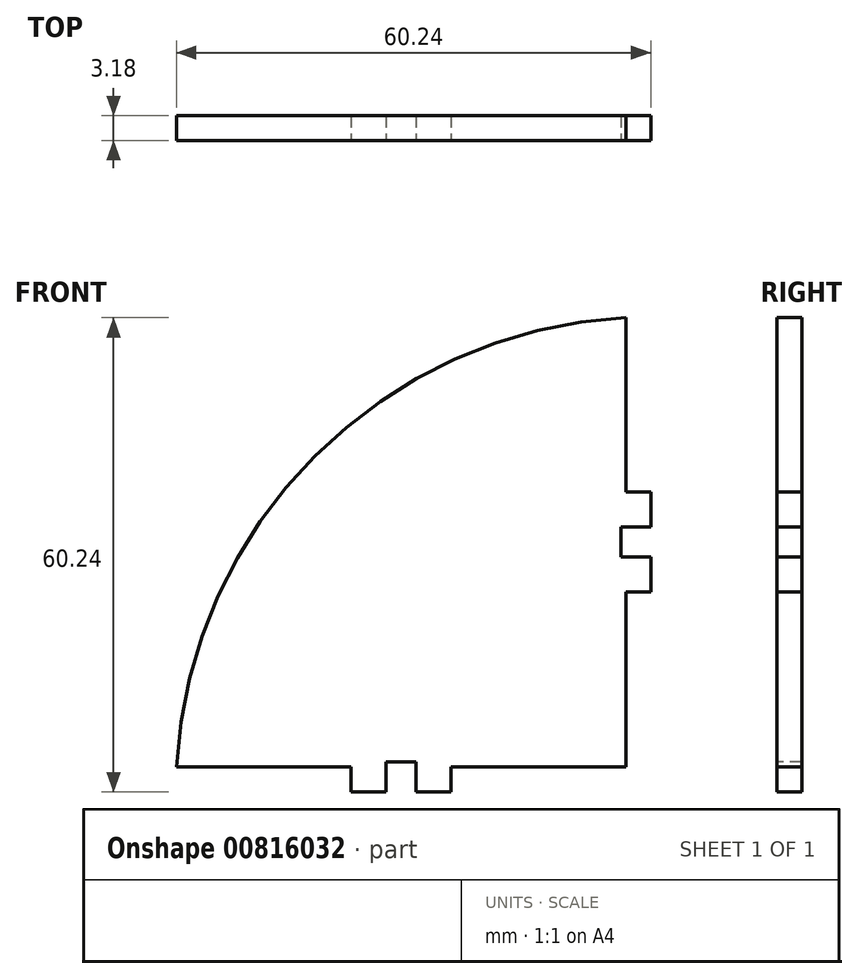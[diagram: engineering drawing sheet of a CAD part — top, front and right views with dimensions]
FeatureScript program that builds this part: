
annotation { "Feature Type Name" : "Feature", "Feature Type Description" : "" }
export const myFeature = defineFeature(function(context is Context, id is Id, definition is map)
    precondition{}
    {
        {
            var Q0;
            Q0=qCreatedBy(makeId("Front.planeOp"),FACE);
            var sketch = newSketch(context, id + "F0", { "sketchPlane" : qUnion([Q0])});
            skLineSegment(sketch, "E0.bottom", {"start": v(0, 0) * mm, "end": v(-60.33, 0) * mm});
            skLineSegment(sketch, "E0.top", {"start": v(0, 60.33) * mm, "end": v(0, 60.33) * mm});
            skLineSegment(sketch, "E0.left", {"start": v(0, 0) * mm, "end": v(0, 60.33) * mm});
            skLineSegment(sketch, "E0.right", {"start": v(-60.33, 0) * mm, "end": v(-60.33, 0) * mm});
            skPoint(sketch, "E1.visualSharp", {"position": v(-60.33, 60.32) * mm});
            skArc(sketch, "E1.filletArc", {"start": v(0, 60.33) * mm, "mid": v(-42.66, 42.66) * mm, "end": v(-60.33, 0) * mm});
            skSolve(sketch);
        }
        {
            var Q0;
            Q0 = qSketchRegion(id + "F0", true);
            extrude(context, id + "F1", {"entities" : qUnion([Q0]), "depth" : 3.17 * mm, "offsetDistance" : 25.4 * mm});
        }
        {
            var Q0;
            Q0=makeQuery(id+"F1.opExtrude","CAP_FACE",FACE,{"disambiguationData":[OSD([sQuery(id+"F0.wireOp",EDGE,"E0.bottom"),sQuery(id+"F0.wireOp",EDGE,"E0.left"),sQuery(id+"F0.wireOp",EDGE,"E1.filletArc")])],"isStart":false});
            var sketch = newSketch(context, id + "F2", { "sketchPlane" : qUnion([Q0])});
            skLineSegment(sketch, "E2.bottom", {"start": v(-60.33, 0) * mm, "end": v(-38.1, 0) * mm});
            skLineSegment(sketch, "E2.top", {"start": v(-60.33, 3.18) * mm, "end": v(-38.1, 3.18) * mm});
            skLineSegment(sketch, "E2.left", {"start": v(-60.33, 0) * mm, "end": v(-60.33, 3.18) * mm});
            skLineSegment(sketch, "E2.right", {"start": v(-38.1, 0) * mm, "end": v(-38.1, 3.18) * mm});
            skLineSegment(sketch, "E3.bottom", {"start": v(0, 0) * mm, "end": v(-25.4, 0) * mm});
            skLineSegment(sketch, "E3.top", {"start": v(0, 3.17) * mm, "end": v(-25.4, 3.17) * mm});
            skLineSegment(sketch, "E3.left", {"start": v(0, 0) * mm, "end": v(0, 3.17) * mm});
            skLineSegment(sketch, "E3.right", {"start": v(-25.4, 0) * mm, "end": v(-25.4, 3.17) * mm});
            skLineSegment(sketch, "E4.bottom", {"start": v(0, 0) * mm, "end": v(-3.17, 0) * mm});
            skLineSegment(sketch, "E4.top", {"start": v(0, 25.4) * mm, "end": v(-3.18, 25.4) * mm});
            skLineSegment(sketch, "E4.left", {"start": v(0, 0) * mm, "end": v(0, 25.4) * mm});
            skLineSegment(sketch, "E4.right", {"start": v(-3.17, 0) * mm, "end": v(-3.18, 25.4) * mm});
            skLineSegment(sketch, "E5.bottom", {"start": v(0, 60.32) * mm, "end": v(-3.17, 60.32) * mm});
            skLineSegment(sketch, "E5.top", {"start": v(0, 38.1) * mm, "end": v(-3.17, 38.1) * mm});
            skLineSegment(sketch, "E5.left", {"start": v(0, 60.33) * mm, "end": v(0, 38.1) * mm});
            skLineSegment(sketch, "E5.right", {"start": v(-3.17, 60.32) * mm, "end": v(-3.17, 38.1) * mm});
            skLineSegment(sketch, "E6", {"start": v(0, 38.1) * mm, "end": v(0, 31.75) * mm, "construction": true});
            skLineSegment(sketch, "E7", {"start": v(0, 31.75) * mm, "end": v(0, 33.65) * mm});
            skLineSegment(sketch, "E8", {"start": v(0, 33.65) * mm, "end": v(-3.8, 33.65) * mm});
            skLineSegment(sketch, "E9", {"start": v(-3.81, 33.65) * mm, "end": v(-3.81, 31.75) * mm});
            skLineSegment(sketch, "E10", {"start": v(0, 31.75) * mm, "end": v(-3.81, 31.75) * mm, "construction": true});
            skLineSegment(sketch, "E11.MirrorCS", {"start": v(0, 31.75) * mm, "end": v(0, 29.85) * mm});
            skLineSegment(sketch, "E12.MirrorCS", {"start": v(-3.8, 29.85) * mm, "end": v(-3.81, 31.75) * mm});
            skLineSegment(sketch, "E13.MirrorCS", {"start": v(0, 29.85) * mm, "end": v(-3.8, 29.85) * mm});
            skLineSegment(sketch, "E14.MirrorCS", {"start": v(0, 25.4) * mm, "end": v(0, 31.75) * mm, "construction": true});
            skLineSegment(sketch, "E15", {"start": v(-25.4, 0) * mm, "end": v(-31.75, 0) * mm, "construction": true});
            skLineSegment(sketch, "E16", {"start": v(-31.75, 0) * mm, "end": v(-29.84, 0) * mm});
            skLineSegment(sketch, "E17", {"start": v(-29.84, 0) * mm, "end": v(-29.84, 3.8) * mm});
            skLineSegment(sketch, "E18", {"start": v(-29.84, 3.8) * mm, "end": v(-31.75, 3.8) * mm});
            skLineSegment(sketch, "E19", {"start": v(-31.75, 0) * mm, "end": v(-31.75, 3.8) * mm, "construction": true});
            skLineSegment(sketch, "E20.MirrorCS", {"start": v(-33.66, 0) * mm, "end": v(-33.66, 3.8) * mm});
            skLineSegment(sketch, "E21.MirrorCS", {"start": v(-33.66, 3.8) * mm, "end": v(-31.75, 3.8) * mm});
            skLineSegment(sketch, "E22.MirrorCS", {"start": v(-31.75, 0) * mm, "end": v(-33.66, 0) * mm});
            skSolve(sketch);
        }
        {
            var Q0;
            Q0 = qSketchRegion(id + "F2", true);
            extrude(context, id + "F3", {"entities" : qUnion([Q0]), "operationType" : NewBodyOperationType.REMOVE, "oppositeDirection" : true, "depth" : 25.4 * mm, "offsetDistance" : 25.4 * mm});
        }
    });
